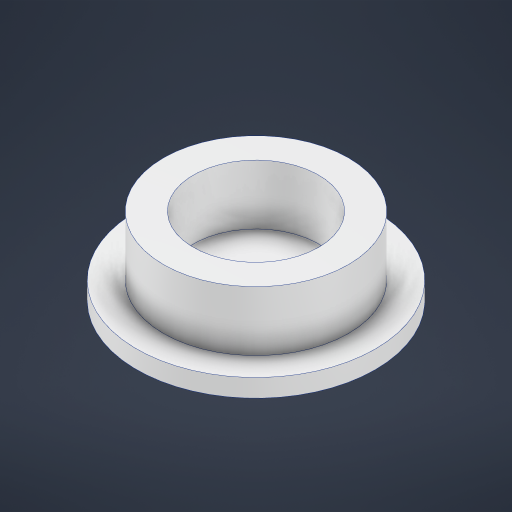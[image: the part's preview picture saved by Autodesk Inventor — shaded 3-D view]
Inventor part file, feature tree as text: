
AUTODESK INVENTOR PART (.ipt)
format: ipt  version: 2024 (Build 280153000, 153)  size: 387,584 bytes
history: native  units: mm
features: extrude x4, sketch x4, pattern_circular x1, projected_geometry x1
ambient origin geometry x8: Origin, YZ Plane, XZ Plane, XY Plane, X Axis, Y Axis, Z Axis, Center Point
bodies: Solid1 (feature_tree)
feature tree (10):
  extrude  "Extrusion1"  Depth=12.0mm TaperAngle=0.0deg
  extrude  "Extrusion2"  Depth=10.0mm TaperAngle=0.0deg
  extrude  "Extrusion3"  Depth=14.0mm TaperAngle=0.0deg
  pattern_circular  "Circular Pattern1"  Count=16  [1 undecoded]
  extrude  "Extrusion4"  [1 undecoded]
  sketch  "Sketch1"  dims[d0=250.0mm d1=12.0mm d2=0.0mm]
  sketch  "Sketch2"  dims[d3=40.0mm d4=0.0mm d5=10.0mm d6=0.0mm]
  projected_geometry  "Projected Loop1"
  sketch  "Sketch3"  dims[d7=1800.0mm d8=360.0deg d10=14.0mm d11=0.0mm d12=160.0mm]
  sketch  "Sketch4"
note: 2 required parameter values undecoded (feature->parameter linkage not recoverable at this tier; creation-order binding heuristic only, values carry confidence <= 0.55)
